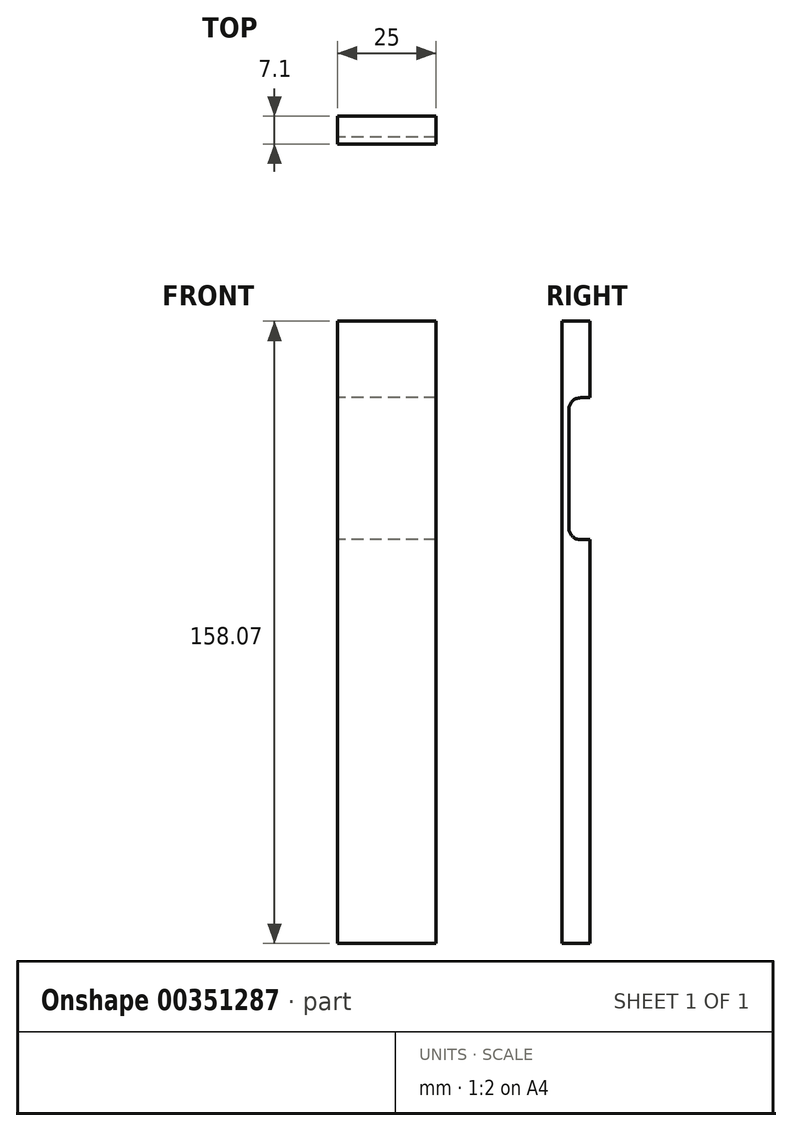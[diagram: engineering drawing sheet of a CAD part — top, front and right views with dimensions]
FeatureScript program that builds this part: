
annotation { "Feature Type Name" : "Feature", "Feature Type Description" : "" }
export const myFeature = defineFeature(function(context is Context, id is Id, definition is map)
    precondition{}
    {
        {
            var Q0;
            Q0=qCreatedBy(makeId("Right.planeOp"),FACE);
            var sketch = newSketch(context, id + "F0", { "sketchPlane" : qUnion([Q0])});
            skLineSegment(sketch, "E0", {"start": v(-49.39, 69.44) * mm, "end": v(-49.39, -88.63) * mm});
            skLineSegment(sketch, "E1", {"start": v(-49.39, -88.63) * mm, "end": v(-42.29, -88.63) * mm});
            skLineSegment(sketch, "E2", {"start": v(-42.29, 69.44) * mm, "end": v(-49.39, 69.44) * mm});
            skLineSegment(sketch, "E3", {"start": v(-42.29, 50) * mm, "end": v(-44.61, 50) * mm});
            skLineSegment(sketch, "E4", {"start": v(-44.61, 13.93) * mm, "end": v(-42.29, 13.93) * mm});
            skLineSegment(sketch, "E5", {"start": v(-47.61, 47) * mm, "end": v(-47.61, 16.93) * mm});
            skPoint(sketch, "E6.visualSharp", {"position": v(-47.61, 50) * mm});
            skArc(sketch, "E6.filletArc", {"start": v(-44.61, 50) * mm, "mid": v(-46.73, 49.11) * mm, "end": v(-47.61, 47) * mm});
            skPoint(sketch, "E7.visualSharp", {"position": v(-47.61, 13.93) * mm});
            skArc(sketch, "E7.filletArc", {"start": v(-47.61, 16.93) * mm, "mid": v(-46.73, 14.8) * mm, "end": v(-44.61, 13.93) * mm});
            skLineSegment(sketch, "E8", {"start": v(-42.29, 50) * mm, "end": v(-42.29, 69.44) * mm});
            skLineSegment(sketch, "E9", {"start": v(-42.29, 13.93) * mm, "end": v(-42.29, -88.63) * mm});
            skSolve(sketch);
        }
        {
            var Q0;
            Q0 = qSketchRegion(id + "F0", true);
            extrude(context, id + "F1", {"entities" : qUnion([Q0]), "depth" : 25 * mm});
        }
    });
